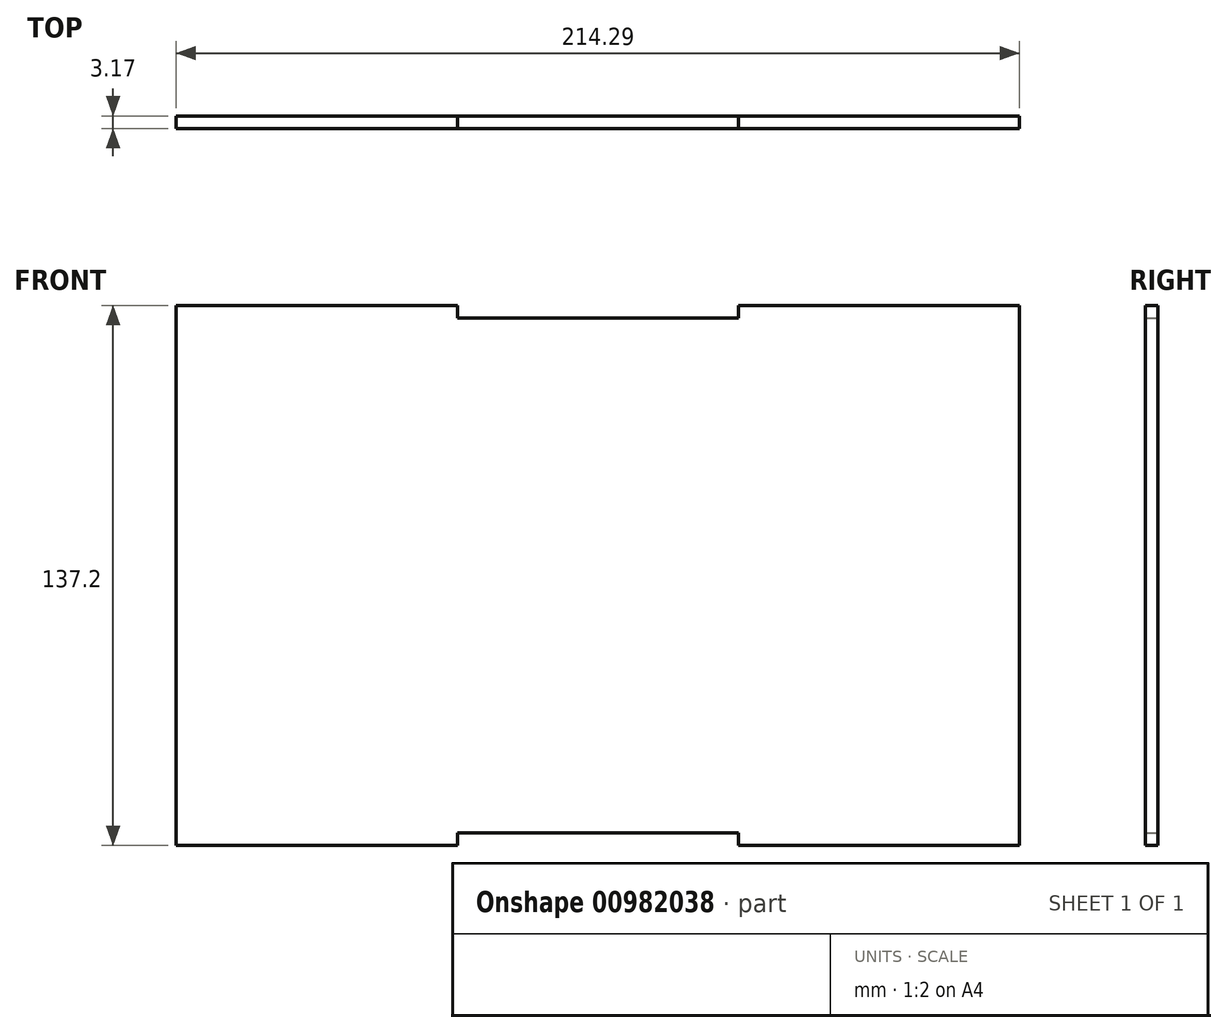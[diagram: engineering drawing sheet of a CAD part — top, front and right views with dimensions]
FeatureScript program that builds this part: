
annotation { "Feature Type Name" : "Feature", "Feature Type Description" : "" }
export const myFeature = defineFeature(function(context is Context, id is Id, definition is map)
    precondition{}
    {
        {
            var Q0;
            Q0=qCreatedBy(makeId("Front.planeOp"),FACE);
            var sketch = newSketch(context, id + "F0", { "sketchPlane" : qUnion([Q0])});
            skLineSegment(sketch, "E0.top", {"start": v(-99.99, -68.6) * mm, "end": v(-28.56, -68.6) * mm});
            skLineSegment(sketch, "E0.left", {"start": v(-99.99, -65.42) * mm, "end": v(-99.99, -68.6) * mm});
            skLineSegment(sketch, "E0.right", {"start": v(-28.56, -65.42) * mm, "end": v(-28.56, -68.6) * mm});
            skLineSegment(sketch, "E1.bottom", {"start": v(-28.56, -65.42) * mm, "end": v(42.87, -65.42) * mm});
            skLineSegment(sketch, "E2.1.0.0", {"start": v(42.87, -68.6) * mm, "end": v(114.3, -68.6) * mm});
            skLineSegment(sketch, "E2.1.0.2", {"start": v(42.87, -65.42) * mm, "end": v(42.87, -68.6) * mm});
            skLineSegment(sketch, "E2.direction1", {"start": v(-99.99, -68.6) * mm, "end": v(42.87, -68.6) * mm, "construction": true});
            skLineSegment(sketch, "E3.MirrorCS", {"start": v(-28.56, 65.42) * mm, "end": v(-28.56, 68.6) * mm});
            skLineSegment(sketch, "E4.MirrorCS", {"start": v(42.87, 65.42) * mm, "end": v(42.87, 68.6) * mm});
            skLineSegment(sketch, "E5.MirrorCS", {"start": v(-99.99, 68.6) * mm, "end": v(-28.56, 68.6) * mm});
            skLineSegment(sketch, "E6.MirrorCS", {"start": v(-28.56, 65.42) * mm, "end": v(42.87, 65.42) * mm});
            skLineSegment(sketch, "E7.MirrorCS", {"start": v(-99.99, 68.6) * mm, "end": v(42.87, 68.6) * mm, "construction": true});
            skLineSegment(sketch, "E8.MirrorCS", {"start": v(42.87, 68.6) * mm, "end": v(114.3, 68.6) * mm});
            skLineSegment(sketch, "E9", {"start": v(-99.99, 68.6) * mm, "end": v(-99.99, -65.42) * mm});
            skLineSegment(sketch, "E10", {"start": v(114.3, 68.6) * mm, "end": v(114.3, -68.6) * mm});
            skSolve(sketch);
        }
        {
            var Q0;
            Q0 = qSketchRegion(id + "F0", true);
            extrude(context, id + "F1", {"entities" : qUnion([Q0]), "depth" : 3.17 * mm, "offsetDistance" : 25.4 * mm});
        }
    });
